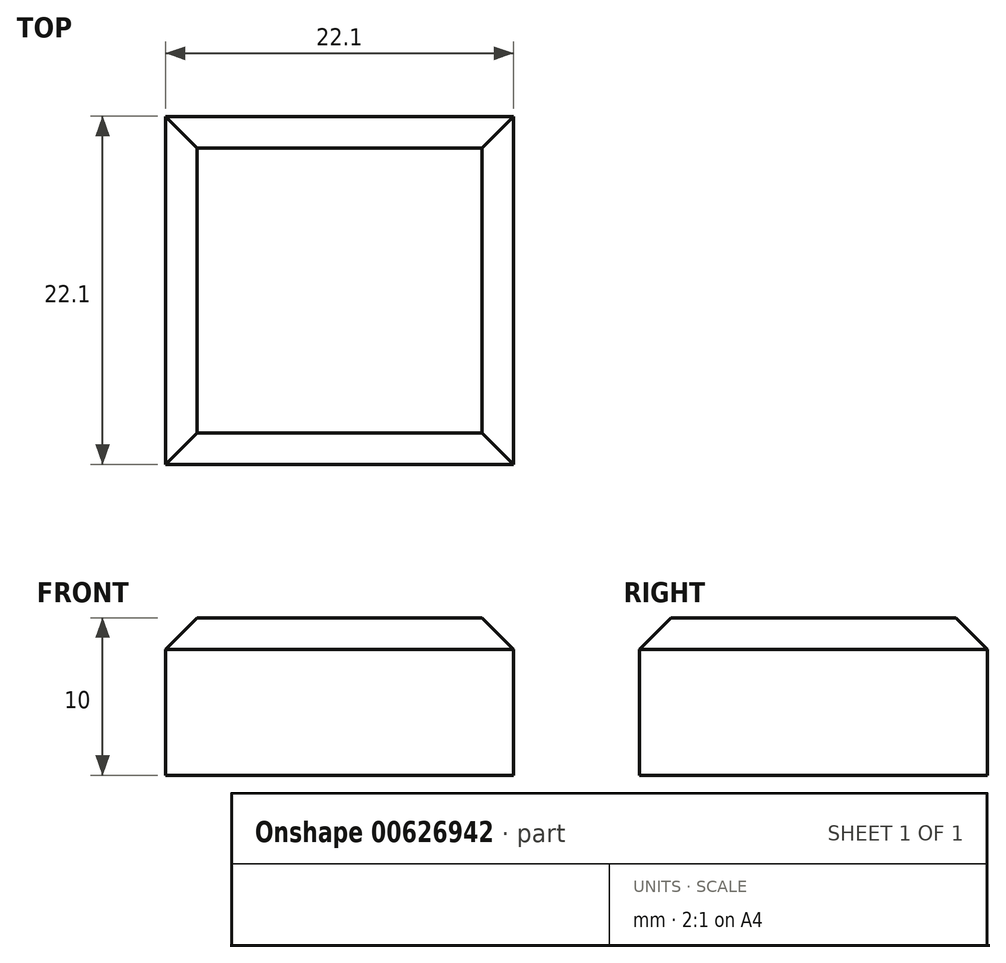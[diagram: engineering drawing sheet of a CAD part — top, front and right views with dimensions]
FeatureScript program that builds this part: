
annotation { "Feature Type Name" : "Feature", "Feature Type Description" : "" }
export const myFeature = defineFeature(function(context is Context, id is Id, definition is map)
    precondition{}
    {
        {
            var Q0;
            Q0=qCreatedBy(makeId("Top.planeOp"),FACE);
            var sketch = newSketch(context, id + "F0", { "sketchPlane" : qUnion([Q0])});
            skLineSegment(sketch, "E0.bottom", {"start": v(0, 0) * mm, "end": v(25.4, 0) * mm});
            skLineSegment(sketch, "E0.top", {"start": v(0, 25.4) * mm, "end": v(25.4, 25.4) * mm});
            skLineSegment(sketch, "E0.left", {"start": v(0, 0) * mm, "end": v(0, 25.4) * mm});
            skLineSegment(sketch, "E0.right", {"start": v(25.4, 0) * mm, "end": v(25.4, 25.4) * mm});
            skLineSegment(sketch, "E1.0", {"start": v(1.65, 1.65) * mm, "end": v(1.65, 23.75) * mm});
            skLineSegment(sketch, "E1.1", {"start": v(1.65, 1.65) * mm, "end": v(23.75, 1.65) * mm});
            skLineSegment(sketch, "E1.2", {"start": v(23.75, 1.65) * mm, "end": v(23.75, 23.75) * mm});
            skLineSegment(sketch, "E1.3", {"start": v(1.65, 23.75) * mm, "end": v(23.75, 23.75) * mm});
            skSolve(sketch);
        }
        {
            var Q0;
            Q0=makeQuery(id+"F0.imprint","IMPRINT",FACE,{"disambiguationData":[TD([[makeQuery(id+"F0.imprint","IMPRINT",EDGE,{"derivedFrom":sQuery(id+"F0.wireOp",EDGE,"E1.0")}),-1.0]])]});
            extrude(context, id + "F1", {"entities" : qUnion([Q0]), "depth" : 10 * mm, "offsetDistance" : 25 * mm});
        }
        {
            var Q0;
            Q0=makeQuery(id+"F1.opExtrude","CAP_EDGE",EDGE,{"disambiguationData":[OSD([sQuery(id+"F0.wireOp",EDGE,"E1.1")])],"isStart":false});
            var Q1;
            Q1=makeQuery(id+"F1.opExtrude","CAP_EDGE",EDGE,{"disambiguationData":[OSD([sQuery(id+"F0.wireOp",EDGE,"E1.0")])],"isStart":false});
            var Q2;
            Q2=makeQuery(id+"F1.opExtrude","CAP_EDGE",EDGE,{"disambiguationData":[OSD([sQuery(id+"F0.wireOp",EDGE,"E1.3")])],"isStart":false});
            var Q3;
            Q3=makeQuery(id+"F1.opExtrude","CAP_EDGE",EDGE,{"disambiguationData":[OSD([sQuery(id+"F0.wireOp",EDGE,"E1.2")])],"isStart":false});
            chamfer(context, id + "F2", {"entities" : qUnion([Q0, Q1, Q2, Q3]), "width" : 2 * mm, "tangentPropagation" : true});
        }
    });
